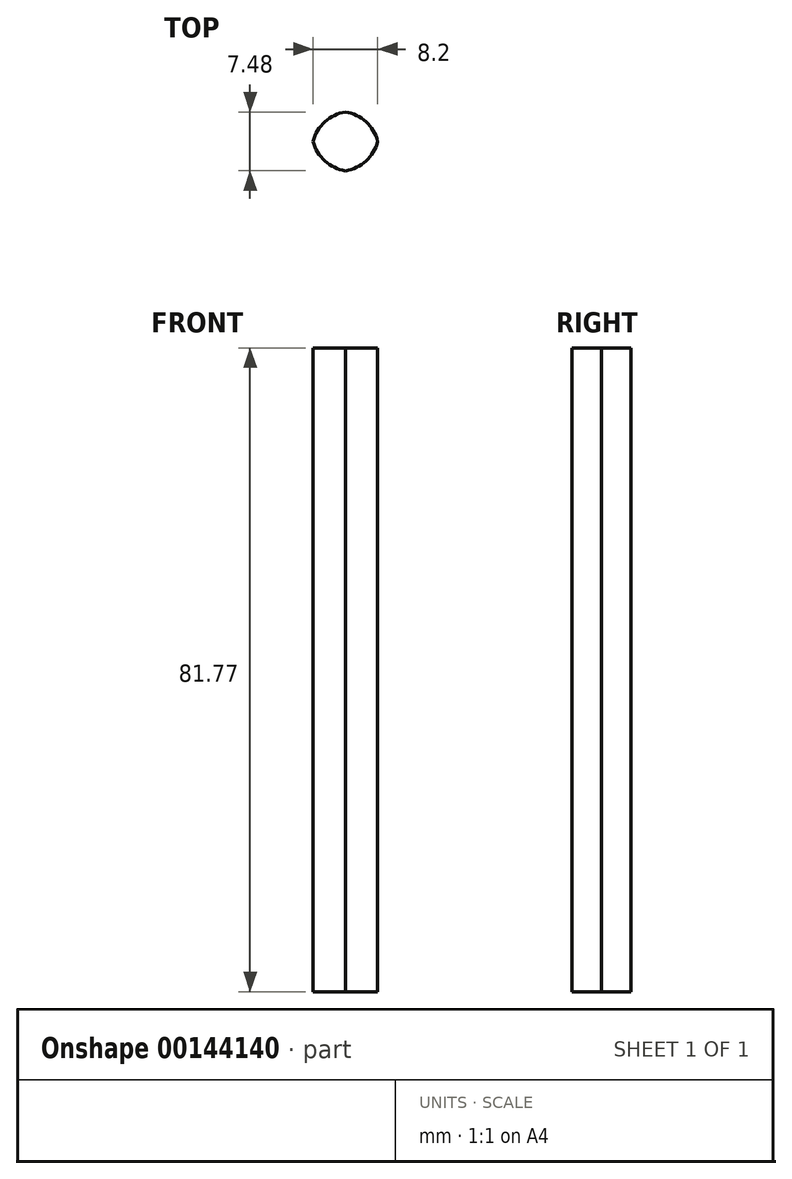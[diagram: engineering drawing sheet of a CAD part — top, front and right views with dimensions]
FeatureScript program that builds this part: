
annotation { "Feature Type Name" : "Feature", "Feature Type Description" : "" }
export const myFeature = defineFeature(function(context is Context, id is Id, definition is map)
    precondition{}
    {
        {
            var Q0;
            Q0=qCreatedBy(makeId("Front.planeOp"),FACE);
            var sketch = newSketch(context, id + "F0", { "sketchPlane" : qUnion([Q0])});
            skLineSegment(sketch, "E0.bottom", {"start": v(-4.1, -42) * mm, "end": v(4.42, -42) * mm});
            skLineSegment(sketch, "E0.top", {"start": v(-4.1, 39.77) * mm, "end": v(4.42, 39.77) * mm});
            skLineSegment(sketch, "E0.left", {"start": v(-4.1, -42) * mm, "end": v(-4.1, 39.77) * mm});
            skLineSegment(sketch, "E0.right", {"start": v(4.42, -42) * mm, "end": v(4.42, 39.77) * mm});
            skSolve(sketch);
        }
        {
            var Q0;
            Q0 = qSketchRegion(id + "F0", true);
            extrude(context, id + "F1", {"entities" : qUnion([Q0]), "endBound" : BoundingType.SYMMETRIC, "depth" : 7.62 * mm});
        }
        {
            var Q0;
            Q0=makeQuery(id+"F1.opExtrude","CAP_EDGE",EDGE,{"disambiguationData":[OSD([sQuery(id+"F0.wireOp",EDGE,"E0.right")])],"isStart":false});
            var Q1;
            Q1=makeQuery(id+"F1.opExtrude","CAP_EDGE",EDGE,{"disambiguationData":[OSD([sQuery(id+"F0.wireOp",EDGE,"E0.right")])],"isStart":true});
            var Q2;
            Q2=makeQuery(id+"F1.opExtrude","CAP_EDGE",EDGE,{"disambiguationData":[OSD([sQuery(id+"F0.wireOp",EDGE,"E0.left")])],"isStart":false});
            var Q3;
            Q3=makeQuery(id+"F1.opExtrude","CAP_EDGE",EDGE,{"disambiguationData":[OSD([sQuery(id+"F0.wireOp",EDGE,"E0.left")])],"isStart":true});
            fillet(context, id + "F2", {"entities" : qUnion([Q0, Q1, Q2, Q3]), "radius" : 5.08 * mm, "tangentPropagation" : true, "allowEdgeOverflow" : false});
        }
    });
